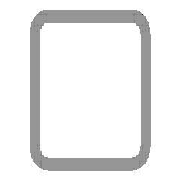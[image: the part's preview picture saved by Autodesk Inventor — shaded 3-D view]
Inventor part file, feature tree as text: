
AUTODESK INVENTOR PART (.ipt)
format: ipt  version: 2025.1 (Build 291241020, 241B)  size: 145,920 bytes
history: native  units: mm (DEFAULTED — no unit token found)
features: other x4, sketch x1, plane x1
ambient origin geometry x8: Origin, YZ Plane, XZ Plane, XY Plane, X Axis, Y Axis, Z Axis, Center Point
bodies: Solid1 (feature_tree), Body (feature_tree)
feature tree (6):
  parser-record x1  (decoder bookkeeping rows leaked as tree rows — omitted from the tree; the rows remain in map.json)
  other  "Driven Length"
  other  "Start plane"
  other  "End plane"
  sketch  "Sketch3"  dims[d3=2200.0mm d4=0.0mm d7=6.0mm d9=100.0mm d11=100.0mm d12=3.0mm d13=100.0mm d14=2300.0mm d15=50.0mm d16=50.0mm d17=90.0deg d18=2200.0mm]
  plane  "Work Plane3"
